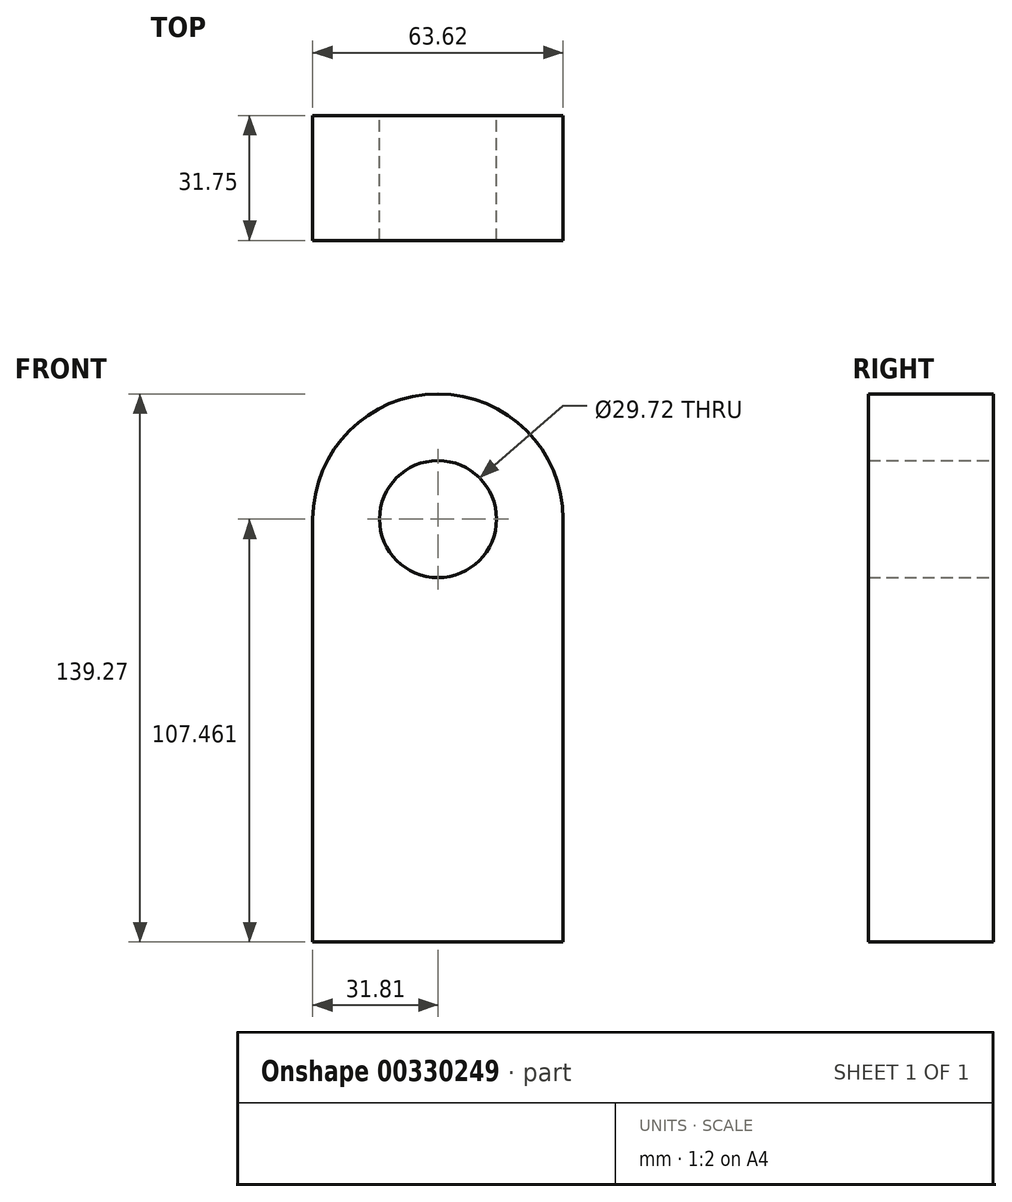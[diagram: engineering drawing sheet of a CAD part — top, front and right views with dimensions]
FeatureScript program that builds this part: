
annotation { "Feature Type Name" : "Feature", "Feature Type Description" : "" }
export const myFeature = defineFeature(function(context is Context, id is Id, definition is map)
    precondition{}
    {
        {
            var Q0;
            Q0=qCreatedBy(makeId("Front.planeOp"),FACE);
            var sketch = newSketch(context, id + "F0", { "sketchPlane" : qUnion([Q0])});
            skLineSegment(sketch, "E0.bottom", {"start": v(31.8, -53.73) * mm, "end": v(-31.8, -53.73) * mm});
            skLineSegment(sketch, "E0.left", {"start": v(31.8, -53.73) * mm, "end": v(31.8, 53.73) * mm});
            skLineSegment(sketch, "E0.right", {"start": v(-31.8, -53.73) * mm, "end": v(-31.8, 53.73) * mm});
            skPoint(sketch, "E0.middle", {"position": v(0, 0) * mm});
            skArc(sketch, "E1", {"start": v(-31.8, 53.73) * mm, "mid": v(0, 85.54) * mm, "end": v(31.8, 53.73) * mm});
            skCircle(sketch, "E2", {"center": v(0, 53.73) * mm, "radius": 14.86 * mm});
            skSolve(sketch);
        }
        {
            var Q0;
            Q0=makeQuery(id+"F0.imprint","IMPRINT",FACE,{"disambiguationData":[TD([[makeQuery(id+"F0.imprint","IMPRINT",EDGE,{"derivedFrom":sQuery(id+"F0.wireOp",EDGE,"E0.bottom")}),-1.0]])]});
            extrude(context, id + "F1", {"entities" : qUnion([Q0]), "depth" : 31.75 * mm});
        }
    });
